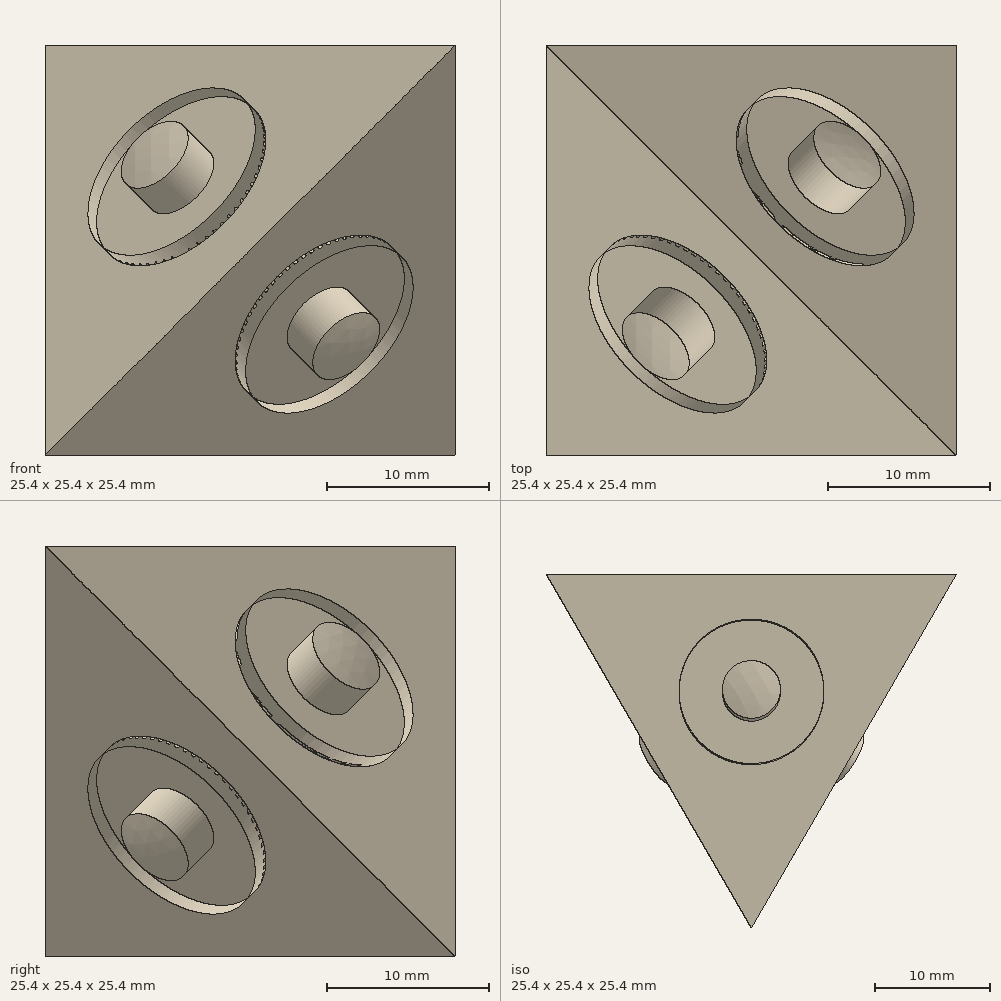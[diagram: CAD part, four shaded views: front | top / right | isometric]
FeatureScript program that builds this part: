
annotation { "Feature Type Name" : "Feature", "Feature Type Description" : "" }
export const myFeature = defineFeature(function(context is Context, id is Id, definition is map)
    precondition{}
    {
        {
            assignVariable(context, id + "F0", {"name" : "d", "anyValue" : .2});
        }
        {
            var Q0;
            Q0=qCreatedBy(makeId("Front.planeOp"),FACE);
            var sketch = newSketch(context, id + "F1", { "sketchPlane" : qUnion([Q0])});
            skCircle(sketch, "E0", {"center": v(0, 0) * mm, "radius": 10.58 * mm});
            skSolve(sketch);
        }
        {
            var Q0;
            Q0=qCreatedBy(makeId("Right.planeOp"),FACE);
            var sketch = newSketch(context, id + "F2", { "sketchPlane" : qUnion([Q0])});
            skCircle(sketch, "E1", {"center": v(0, 0) * mm, "radius": 10.58 * mm});
            skSolve(sketch);
        }
        {
            var Q0;
            Q0=qCreatedBy(makeId("Front.planeOp"),FACE);
            var sketch = newSketch(context, id + "F3", { "sketchPlane" : qUnion([Q0])});
            skLineSegment(sketch, "E2.bottom", {"start": v(12.7, -12.7) * mm, "end": v(-12.7, -12.7) * mm});
            skLineSegment(sketch, "E2.top", {"start": v(12.7, 12.7) * mm, "end": v(-12.7, 12.7) * mm});
            skLineSegment(sketch, "E2.left", {"start": v(12.7, -12.7) * mm, "end": v(12.7, 12.7) * mm});
            skLineSegment(sketch, "E2.right", {"start": v(-12.7, -12.7) * mm, "end": v(-12.7, 12.7) * mm});
            skPoint(sketch, "E2.middle", {"position": v(0, 0) * mm});
            skSolve(sketch);
        }
        {
            var Q0;
            Q0=makeQuery(id+"F3.imprint","IMPRINT",FACE,{"disambiguationData":[TD([[makeQuery(id+"F3.imprint","IMPRINT",EDGE,{"derivedFrom":sQuery(id+"F3.wireOp",EDGE,"E2.bottom")}),-1.0]])]});
            extrude(context, id + "F4", {"entities" : qUnion([Q0]), "endBound" : BoundingType.SYMMETRIC, "depth" : 25.4 * mm, "offsetDistance" : 25.4 * mm});
        }
        {
            var Q0;
            Q0=makeQuery(id+"F4.opExtrude","SWEPT_FACE",FACE,{"disambiguationData":[OSD([sQuery(id+"F3.wireOp",EDGE,"E2.right")])]});
            var sketch = newSketch(context, id + "F5", { "sketchPlane" : qUnion([Q0])});
            skLineSegment(sketch, "E3", {"start": v(-12.7, 12.7) * mm, "end": v(12.7, -12.7) * mm});
            skSolve(sketch);
        }
        {
            var Q0;
            Q0=makeQuery(id+"F4.opExtrude","CAP_FACE",FACE,{"disambiguationData":[OSD([sQuery(id+"F3.wireOp",EDGE,"E2.bottom"),sQuery(id+"F3.wireOp",EDGE,"E2.top"),sQuery(id+"F3.wireOp",EDGE,"E2.left"),sQuery(id+"F3.wireOp",EDGE,"E2.right")])],"isStart":false});
            var sketch = newSketch(context, id + "F6", { "sketchPlane" : qUnion([Q0])});
            skLineSegment(sketch, "E4", {"start": v(-12.7, -12.7) * mm, "end": v(12.7, 12.7) * mm});
            skSolve(sketch);
        }
        {
            var Q0;
            Q0=makeQuery(id+"F4.opExtrude","CAP_FACE",FACE,{"disambiguationData":[OSD([sQuery(id+"F3.wireOp",EDGE,"E2.bottom"),sQuery(id+"F3.wireOp",EDGE,"E2.top"),sQuery(id+"F3.wireOp",EDGE,"E2.left"),sQuery(id+"F3.wireOp",EDGE,"E2.right")])],"isStart":true});
            var sketch = newSketch(context, id + "F7", { "sketchPlane" : qUnion([Q0])});
            skLineSegment(sketch, "E5", {"start": v(12.7, 12.7) * mm, "end": v(-12.7, -12.7) * mm});
            skSolve(sketch);
        }
        {
            var Q0;
            Q0=makeQuery(id+"F4.opExtrude","SWEPT_FACE",FACE,{"disambiguationData":[OSD([sQuery(id+"F3.wireOp",EDGE,"E2.bottom")])]});
            var sketch = newSketch(context, id + "F8", { "sketchPlane" : qUnion([Q0])});
            skLineSegment(sketch, "E6", {"start": v(-12.7, 12.7) * mm, "end": v(12.7, -12.7) * mm});
            skSolve(sketch);
        }
        {
            var Q0;
            Q0=sQuery(id+"F7.wireOp",VERTEX,"E5.start");
            var Q1;
            Q1=sQuery(id+"F8.wireOp",VERTEX,"E6.end");
            var Q2;
            Q2=sQuery(id+"F5.wireOp",VERTEX,"E3.end");
            cPlane(context, id + "F9", {"entities" : qUnion([Q0, Q1, Q2]), "cplaneType" : CPlaneType.THREE_POINT, "offset" : 25.4 * mm, "width" : 152.4 * mm, "height" : 152.4 * mm});
        }
        {
            var Q0;
            Q0=qCreatedBy(id+"F9.planeOp",FACE);
            var sketch = newSketch(context, id + "F10", { "sketchPlane" : qUnion([Q0])});
            skLineSegment(sketch, "E7.bottom", {"start": v(31.97, 29.26) * mm, "end": v(-31.97, 29.26) * mm});
            skLineSegment(sketch, "E7.top", {"start": v(31.97, -34.1) * mm, "end": v(-31.97, -34.1) * mm});
            skLineSegment(sketch, "E7.left", {"start": v(31.97, 29.26) * mm, "end": v(31.97, -34.1) * mm});
            skLineSegment(sketch, "E7.right", {"start": v(-31.97, 29.26) * mm, "end": v(-31.97, -34.1) * mm});
            skPoint(sketch, "E7.middle", {"position": v(0, -2.42) * mm});
            skSolve(sketch);
        }
        {
            var Q0;
            Q0=makeQuery(id+"F10.imprint","IMPRINT",FACE,{"disambiguationData":[TD([[makeQuery(id+"F10.imprint","IMPRINT",EDGE,{"derivedFrom":sQuery(id+"F10.wireOp",EDGE,"E7.bottom")}),1.0]])]});
            extrude(context, id + "F11", {"entities" : qUnion([Q0]), "operationType" : NewBodyOperationType.REMOVE, "oppositeDirection" : true, "depth" : 25.4 * mm, "offsetDistance" : 25.4 * mm});
        }
        {
            var Q0;
            Q0=sQuery(id+"F5.wireOp",VERTEX,"E3.end");
            var Q1;
            Q1=sQuery(id+"F7.wireOp",VERTEX,"E5.start");
            var Q2;
            Q2=sQuery(id+"F6.wireOp",VERTEX,"E4.end");
            cPlane(context, id + "F12", {"entities" : qUnion([Q0, Q1, Q2]), "cplaneType" : CPlaneType.THREE_POINT, "offset" : 25.4 * mm, "width" : 152.4 * mm, "height" : 152.4 * mm});
        }
        {
            var Q0;
            Q0=qCreatedBy(id+"F12.planeOp",FACE);
            var sketch = newSketch(context, id + "F13", { "sketchPlane" : qUnion([Q0])});
            skLineSegment(sketch, "E8.bottom", {"start": v(34.62, 31.3) * mm, "end": v(-34.62, 31.3) * mm});
            skLineSegment(sketch, "E8.top", {"start": v(34.62, -31.3) * mm, "end": v(-34.62, -31.3) * mm});
            skLineSegment(sketch, "E8.left", {"start": v(34.62, 31.3) * mm, "end": v(34.62, -31.3) * mm});
            skLineSegment(sketch, "E8.right", {"start": v(-34.62, 31.3) * mm, "end": v(-34.62, -31.3) * mm});
            skPoint(sketch, "E8.middle", {"position": v(0, 0) * mm});
            skSolve(sketch);
        }
        {
            var Q0;
            Q0=makeQuery(id+"F13.imprint","IMPRINT",FACE,{"disambiguationData":[TD([[makeQuery(id+"F13.imprint","IMPRINT",EDGE,{"derivedFrom":sQuery(id+"F13.wireOp",EDGE,"E8.bottom")}),1.0]])]});
            extrude(context, id + "F14", {"entities" : qUnion([Q0]), "operationType" : NewBodyOperationType.REMOVE, "depth" : 25.4 * mm, "offsetDistance" : 25.4 * mm});
        }
        {
            var Q0;
            Q0=sQuery(id+"F6.wireOp",VERTEX,"E4.end");
            var Q1;
            Q1=sQuery(id+"F8.wireOp",VERTEX,"E6.end");
            var Q2;
            Q2=sQuery(id+"F7.wireOp",VERTEX,"E5.start");
            cPlane(context, id + "F15", {"entities" : qUnion([Q0, Q1, Q2]), "cplaneType" : CPlaneType.THREE_POINT, "offset" : 25.4 * mm, "width" : 152.4 * mm, "height" : 152.4 * mm});
        }
        {
            var Q0;
            Q0=qCreatedBy(id+"F15.planeOp",FACE);
            var sketch = newSketch(context, id + "F16", { "sketchPlane" : qUnion([Q0])});
            skLineSegment(sketch, "E9.bottom", {"start": v(41.74, -29.23) * mm, "end": v(-41.74, -29.23) * mm});
            skLineSegment(sketch, "E9.top", {"start": v(41.74, 32.56) * mm, "end": v(-41.74, 32.56) * mm});
            skLineSegment(sketch, "E9.left", {"start": v(41.74, -29.23) * mm, "end": v(41.74, 32.56) * mm});
            skLineSegment(sketch, "E9.right", {"start": v(-41.74, -29.23) * mm, "end": v(-41.74, 32.56) * mm});
            skPoint(sketch, "E9.middle", {"position": v(0, 1.66) * mm});
            skSolve(sketch);
        }
        {
            var Q0;
            Q0=makeQuery(id+"F16.imprint","IMPRINT",FACE,{"disambiguationData":[TD([[makeQuery(id+"F16.imprint","IMPRINT",EDGE,{"derivedFrom":sQuery(id+"F16.wireOp",EDGE,"E9.bottom")}),-1.0]])]});
            extrude(context, id + "F17", {"entities" : qUnion([Q0]), "operationType" : NewBodyOperationType.REMOVE, "oppositeDirection" : true, "depth" : 25.4 * mm, "offsetDistance" : 25.4 * mm});
        }
        {
            var Q0;
            Q0=sQuery(id+"F5.wireOp",VERTEX,"E3.end");
            var Q1;
            Q1=sQuery(id+"F6.wireOp",VERTEX,"E4.end");
            var Q2;
            Q2=sQuery(id+"F8.wireOp",VERTEX,"E6.end");
            cPlane(context, id + "F18", {"entities" : qUnion([Q0, Q1, Q2]), "cplaneType" : CPlaneType.THREE_POINT, "offset" : 25.4 * mm, "width" : 152.4 * mm, "height" : 152.4 * mm});
        }
        {
            var Q0;
            Q0=qCreatedBy(id+"F18.planeOp",FACE);
            var sketch = newSketch(context, id + "F19", { "sketchPlane" : qUnion([Q0])});
            skLineSegment(sketch, "E10.bottom", {"start": v(47.99, -32.73) * mm, "end": v(-47.99, -32.73) * mm});
            skLineSegment(sketch, "E10.top", {"start": v(47.99, 32.73) * mm, "end": v(-47.99, 32.73) * mm});
            skLineSegment(sketch, "E10.left", {"start": v(47.99, -32.73) * mm, "end": v(47.99, 32.73) * mm});
            skLineSegment(sketch, "E10.right", {"start": v(-47.99, -32.73) * mm, "end": v(-47.99, 32.73) * mm});
            skPoint(sketch, "E10.middle", {"position": v(0, 0) * mm});
            skSolve(sketch);
        }
        {
            var Q0;
            Q0=makeQuery(id+"F19.imprint","IMPRINT",FACE,{"disambiguationData":[TD([[makeQuery(id+"F19.imprint","IMPRINT",EDGE,{"derivedFrom":sQuery(id+"F19.wireOp",EDGE,"E10.bottom")}),-1.0]])]});
            extrude(context, id + "F20", {"entities" : qUnion([Q0]), "operationType" : NewBodyOperationType.REMOVE, "depth" : 25.4 * mm, "offsetDistance" : 25.4 * mm});
        }
        {
            var Q0;
            Q0=makeQuery(id+"F1.imprint","IMPRINT",FACE,{"disambiguationData":[TD([[makeQuery(id+"F1.imprint","IMPRINT",EDGE,{"derivedFrom":sQuery(id+"F1.wireOp",EDGE,"E0")}),1.0]])]});
            var Q1;
            Q1=sQuery(id+"F2.wireOp",EDGE,"E1");
            sweep(context, id + "F21", {"profiles" : qUnion([Q0]), "path" : qUnion([Q1])});
        }
        {
            var Q0;
            Q0=qCreatedBy(id+"F18.planeOp",FACE);
            var sketch = newSketch(context, id + "F22", { "sketchPlane" : qUnion([Q0])});
            skCircle(sketch, "E11", {"center": v(0, 0) * mm, "radius": 6.35 * mm});
            skCircle(sketch, "E12", {"center": v(0, 0) * mm, "radius": 2.54 * mm});
            skSolve(sketch);
        }
        {
            var Q0;
            Q0 = qSketchRegion(id + "F22", true);
            extrude(context, id + "F23", {"entities" : qUnion([Q0]), "operationType" : NewBodyOperationType.REMOVE, "depth" : 25.4 * mm, "offsetDistance" : 25.4 * mm});
        }
        {
            var Q0;
            Q0=qCreatedBy(id+"F15.planeOp",FACE);
            var sketch = newSketch(context, id + "F24", { "sketchPlane" : qUnion([Q0])});
            skCircle(sketch, "E13", {"center": v(0, 0) * mm, "radius": 6.35 * mm});
            skCircle(sketch, "E14", {"center": v(0, 0) * mm, "radius": 2.54 * mm});
            skSolve(sketch);
        }
        {
            var Q0;
            Q0=qCreatedBy(id+"F12.planeOp",FACE);
            var sketch = newSketch(context, id + "F25", { "sketchPlane" : qUnion([Q0])});
            skCircle(sketch, "E15", {"center": v(0, 0) * mm, "radius": 6.35 * mm});
            skCircle(sketch, "E16", {"center": v(0, 0) * mm, "radius": 2.54 * mm});
            skSolve(sketch);
        }
        {
            var Q0;
            Q0=qCreatedBy(id+"F9.planeOp",FACE);
            var sketch = newSketch(context, id + "F26", { "sketchPlane" : qUnion([Q0])});
            skCircle(sketch, "E17", {"center": v(0, 0) * mm, "radius": 6.35 * mm});
            skCircle(sketch, "E18", {"center": v(0, 0) * mm, "radius": 2.54 * mm});
            skSolve(sketch);
        }
        {
            var Q0;
            Q0 = qSketchRegion(id + "F24", true);
            extrude(context, id + "F27", {"entities" : qUnion([Q0]), "operationType" : NewBodyOperationType.REMOVE, "oppositeDirection" : true, "depth" : 25.4 * mm, "offsetDistance" : 25.4 * mm});
        }
        {
            var Q0;
            Q0 = qSketchRegion(id + "F25", true);
            extrude(context, id + "F28", {"entities" : qUnion([Q0]), "operationType" : NewBodyOperationType.REMOVE, "depth" : 25.4 * mm, "offsetDistance" : 25.4 * mm});
        }
        {
            var Q0;
            Q0 = qSketchRegion(id + "F26", true);
            extrude(context, id + "F29", {"entities" : qUnion([Q0]), "operationType" : NewBodyOperationType.REMOVE, "oppositeDirection" : true, "depth" : 25.4 * mm, "offsetDistance" : 25.4 * mm});
        }
        {
            var Q0;
            Q0=makeQuery(id+"F11.boolean.opBoolean","COPY",FACE,{"derivedFrom":makeQuery(id+"F11.opExtrude","CAP_FACE",FACE,{"disambiguationData":[OSD([sQuery(id+"F10.wireOp",EDGE,"E7.bottom"),sQuery(id+"F10.wireOp",EDGE,"E7.top"),sQuery(id+"F10.wireOp",EDGE,"E7.left"),sQuery(id+"F10.wireOp",EDGE,"E7.right")])],"isStart":true})});
            var sketch = newSketch(context, id + "F30", { "sketchPlane" : qUnion([Q0])});
            skLineSegment(sketch, "E19", {"start": v(20.74, 0) * mm, "end": v(-10.37, 17.96) * mm});
            skLineSegment(sketch, "E20", {"start": v(-10.37, 17.96) * mm, "end": v(-10.37, -17.96) * mm});
            skLineSegment(sketch, "E21", {"start": v(-10.37, -17.96) * mm, "end": v(20.74, 0) * mm});
            skSolve(sketch);
        }
        {
            var Q0;
            Q0=sQuery(id+"F30.wireOp",EDGE,"E19");
            var Q1;
            Q1=sQuery(id+"F30.wireOp",VERTEX,"E20.end");
            loft(context, id + "F31", {"bodyType" : ToolBodyType.SURFACE, "wireProfilesArray" : [{ "wireProfileEntities" : qUnion([Q0]) }, { "wireProfileEntities" : qUnion([Q1]) }]});
        }
        {
            var Q0;
            Q0 = qSketchRegion(id + "F24", true);
            extrude(context, id + "F32", {"entities" : qUnion([Q0]), "oppositeDirection" : true, "depth" : (getVariable(context, 'd')) * mm, "offsetDistance" : 25.4 * mm});
        }
        {
            var Q0;
            Q0 = qSketchRegion(id + "F25", true);
            extrude(context, id + "F33", {"entities" : qUnion([Q0]), "depth" : (getVariable(context, 'd')) * mm, "offsetDistance" : 25.4 * mm});
        }
        {
            var Q0;
            Q0 = qSketchRegion(id + "F26", true);
            extrude(context, id + "F34", {"entities" : qUnion([Q0]), "oppositeDirection" : true, "depth" : (getVariable(context, 'd')) * mm, "offsetDistance" : 25.4 * mm});
        }
        {
            var Q0;
            Q0 = qSketchRegion(id + "F22", true);
            extrude(context, id + "F35", {"entities" : qUnion([Q0]), "depth" : (getVariable(context, 'd')) * mm, "offsetDistance" : 25.4 * mm});
        }
        {
            var Q0;
            Q0=makeQuery(id+"F20.boolean.opBoolean","COPY",FACE,{"derivedFrom":makeQuery(id+"F20.opExtrude","CAP_FACE",FACE,{"disambiguationData":[OSD([sQuery(id+"F19.wireOp",EDGE,"E10.bottom"),sQuery(id+"F19.wireOp",EDGE,"E10.top"),sQuery(id+"F19.wireOp",EDGE,"E10.left"),sQuery(id+"F19.wireOp",EDGE,"E10.right")])],"isStart":true})});
            var sketch = newSketch(context, id + "F36", { "sketchPlane" : qUnion([Q0])});
            skLineSegment(sketch, "E22", {"start": v(-10.37, 17.96) * mm, "end": v(-10.37, -17.96) * mm});
            skLineSegment(sketch, "E23", {"start": v(-10.37, -17.96) * mm, "end": v(20.74, 0) * mm});
            skLineSegment(sketch, "E24", {"start": v(20.74, 0) * mm, "end": v(-10.37, 17.96) * mm});
            skSolve(sketch);
        }
        {
            var Q0;
            Q0=sQuery(id+"F36.wireOp",EDGE,"E23");
            var Q1;
            Q1=sQuery(id+"F36.wireOp",VERTEX,"E22.start");
            var Q2;
            Q2=sQuery(id+"F36.wireOp",EDGE,"E24");
            var Q3;
            Q3=sQuery(id+"F36.wireOp",EDGE,"E22");
            loft(context, id + "F37", {"bodyType" : ToolBodyType.SURFACE, "addGuides" : true, "wireProfilesArray" : [{ "wireProfileEntities" : qUnion([Q0]) }, { "wireProfileEntities" : qUnion([Q1]) }], "guidesArray" : [{ "guideEntities" : qUnion([Q2]), "guideDerivativeType" : LoftGuideDerivativeType.DEFAULT, "guideDerivativeMagnitude" : 1 }, { "guideEntities" : qUnion([Q3]), "guideDerivativeType" : LoftGuideDerivativeType.DEFAULT, "guideDerivativeMagnitude" : 1 }]});
        }
        {
            var Q0;
            Q0=makeQuery(id+"F17.boolean.opBoolean","COPY",FACE,{"derivedFrom":makeQuery(id+"F17.opExtrude","CAP_FACE",FACE,{"disambiguationData":[OSD([sQuery(id+"F16.wireOp",EDGE,"E9.bottom"),sQuery(id+"F16.wireOp",EDGE,"E9.top"),sQuery(id+"F16.wireOp",EDGE,"E9.left"),sQuery(id+"F16.wireOp",EDGE,"E9.right")])],"isStart":true})});
            var sketch = newSketch(context, id + "F38", { "sketchPlane" : qUnion([Q0])});
            skLineSegment(sketch, "E25", {"start": v(20.74, 0) * mm, "end": v(-10.37, -17.96) * mm});
            skLineSegment(sketch, "E26", {"start": v(-10.37, -17.96) * mm, "end": v(-10.37, 17.96) * mm});
            skLineSegment(sketch, "E27", {"start": v(20.74, 0) * mm, "end": v(-10.37, 17.96) * mm});
            skSolve(sketch);
        }
        {
            var Q0;
            Q0=sQuery(id+"F38.wireOp",EDGE,"E25");
            var Q1;
            Q1=sQuery(id+"F38.wireOp",VERTEX,"E27.end");
            var Q2;
            Q2=sQuery(id+"F38.wireOp",EDGE,"E27");
            var Q3;
            Q3=sQuery(id+"F38.wireOp",EDGE,"E26");
            loft(context, id + "F39", {"bodyType" : ToolBodyType.SURFACE, "addGuides" : true, "wireProfilesArray" : [{ "wireProfileEntities" : qUnion([Q0]) }, { "wireProfileEntities" : qUnion([Q1]) }], "guidesArray" : [{ "guideEntities" : qUnion([Q2]), "guideDerivativeType" : LoftGuideDerivativeType.DEFAULT, "guideDerivativeMagnitude" : 1 }, { "guideEntities" : qUnion([Q3]), "guideDerivativeType" : LoftGuideDerivativeType.DEFAULT, "guideDerivativeMagnitude" : 1 }]});
        }
        {
            var Q0;
            Q0=sQuery(id+"F38.wireOp",EDGE,"E25");
            var Q1;
            Q1=sQuery(id+"F38.wireOp",VERTEX,"E26.end");
            var Q2;
            Q2=sQuery(id+"F38.wireOp",EDGE,"E27");
            var Q3;
            Q3=sQuery(id+"F38.wireOp",EDGE,"E26");
            loft(context, id + "F40", {"bodyType" : ToolBodyType.SURFACE, "addGuides" : true, "wireProfilesArray" : [{ "wireProfileEntities" : qUnion([Q0]) }, { "wireProfileEntities" : qUnion([Q1]) }], "guidesArray" : [{ "guideEntities" : qUnion([Q2]), "guideDerivativeType" : LoftGuideDerivativeType.DEFAULT, "guideDerivativeMagnitude" : 1 }, { "guideEntities" : qUnion([Q3]), "guideDerivativeType" : LoftGuideDerivativeType.DEFAULT, "guideDerivativeMagnitude" : 1 }]});
        }
        {
            var Q0;
            Q0=makeQuery(id+"F36.imprint","IMPRINT",FACE,{"disambiguationData":[TD([[makeQuery(id+"F36.imprint","IMPRINT",EDGE,{"derivedFrom":sQuery(id+"F36.wireOp",EDGE,"E22")}),1.0]])]});
            var Q1;
            Q1=sQuery(id+"F36.wireOp",EDGE,"E24");
            var Q2;
            Q2=sQuery(id+"F36.wireOp",VERTEX,"E23.start");
            var Q3;
            Q3=sQuery(id+"F36.wireOp",EDGE,"E23");
            var Q4;
            Q4=sQuery(id+"F36.wireOp",EDGE,"E22");
            loft(context, id + "F41", {"bodyType" : ToolBodyType.SURFACE, "addGuides" : true, "sheetProfilesArray" : [{ "sheetProfileEntities" : qUnion([Q0]) }], "wireProfilesArray" : [{ "wireProfileEntities" : qUnion([Q1]) }, { "wireProfileEntities" : qUnion([Q2]) }], "guidesArray" : [{ "guideEntities" : qUnion([Q3]), "guideDerivativeType" : LoftGuideDerivativeType.DEFAULT, "guideDerivativeMagnitude" : 1 }, { "guideEntities" : qUnion([Q4]), "guideDerivativeType" : LoftGuideDerivativeType.DEFAULT, "guideDerivativeMagnitude" : 1 }]});
        }
        {
            var Q0;
            Q0=sQuery(id+"F30.wireOp",VERTEX,"E19.start");
            var Q1;
            Q1=sQuery(id+"F30.wireOp",EDGE,"E19");
            var Q2;
            Q2=sQuery(id+"F30.wireOp",VERTEX,"E21.start");
            var Q3;
            Q3=sQuery(id+"F30.wireOp",EDGE,"E21");
            var Q4;
            Q4=sQuery(id+"F30.wireOp",EDGE,"E20");
            loft(context, id + "F42", {"bodyType" : ToolBodyType.SURFACE, "addGuides" : true, "sheetProfilesArray" : [{ "sheetProfileEntities" : qUnion([Q0]) }], "wireProfilesArray" : [{ "wireProfileEntities" : qUnion([Q1]) }, { "wireProfileEntities" : qUnion([Q2]) }], "guidesArray" : [{ "guideEntities" : qUnion([Q3]), "guideDerivativeType" : LoftGuideDerivativeType.DEFAULT, "guideDerivativeMagnitude" : 1 }, { "guideEntities" : qUnion([Q4]), "guideDerivativeType" : LoftGuideDerivativeType.DEFAULT, "guideDerivativeMagnitude" : 1 }]});
        }
        {
            var Q0;
            Q0=sQuery(id+"F36.wireOp",EDGE,"E24");
            var Q1;
            Q1=sQuery(id+"F36.wireOp",VERTEX,"E23.start");
            var Q2;
            Q2=sQuery(id+"F36.wireOp",EDGE,"E22");
            var Q3;
            Q3=sQuery(id+"F36.wireOp",EDGE,"E23");
            loft(context, id + "F43", {"bodyType" : ToolBodyType.SURFACE, "addGuides" : true, "wireProfilesArray" : [{ "wireProfileEntities" : qUnion([Q0]) }, { "wireProfileEntities" : qUnion([Q1]) }], "guidesArray" : [{ "guideEntities" : qUnion([Q2]), "guideDerivativeType" : LoftGuideDerivativeType.DEFAULT, "guideDerivativeMagnitude" : 1 }, { "guideEntities" : qUnion([Q3]), "guideDerivativeType" : LoftGuideDerivativeType.DEFAULT, "guideDerivativeMagnitude" : 1 }]});
        }
        {
            var Q0;
            Q0=makeQuery(id+"F14.boolean.opBoolean","COPY",FACE,{"derivedFrom":makeQuery(id+"F14.opExtrude","CAP_FACE",FACE,{"disambiguationData":[OSD([sQuery(id+"F13.wireOp",EDGE,"E8.bottom"),sQuery(id+"F13.wireOp",EDGE,"E8.top"),sQuery(id+"F13.wireOp",EDGE,"E8.left"),sQuery(id+"F13.wireOp",EDGE,"E8.right")])],"isStart":true})});
            var sketch = newSketch(context, id + "F44", { "sketchPlane" : qUnion([Q0])});
            skLineSegment(sketch, "E28", {"start": v(-20.74, 0) * mm, "end": v(10.37, -17.96) * mm});
            skLineSegment(sketch, "E29", {"start": v(10.37, -17.96) * mm, "end": v(10.37, 17.96) * mm});
            skLineSegment(sketch, "E30", {"start": v(10.37, 17.96) * mm, "end": v(-20.74, 0) * mm});
            skSolve(sketch);
        }
        {
            var Q0;
            Q0=makeQuery(id+"F44.imprint","IMPRINT",FACE,{"disambiguationData":[TD([[makeQuery(id+"F44.imprint","IMPRINT",EDGE,{"derivedFrom":sQuery(id+"F44.wireOp",EDGE,"E28")}),-1.0]])]});
            var Q1;
            Q1=sQuery(id+"F44.wireOp",EDGE,"E28");
            var Q2;
            Q2=sQuery(id+"F44.wireOp",VERTEX,"E29.end");
            var Q3;
            Q3=sQuery(id+"F44.wireOp",EDGE,"E30");
            var Q4;
            Q4=sQuery(id+"F44.wireOp",EDGE,"E29");
            loft(context, id + "F45", {"bodyType" : ToolBodyType.SURFACE, "addGuides" : true, "sheetProfilesArray" : [{ "sheetProfileEntities" : qUnion([Q0]) }], "wireProfilesArray" : [{ "wireProfileEntities" : qUnion([Q1]) }, { "wireProfileEntities" : qUnion([Q2]) }], "guidesArray" : [{ "guideEntities" : qUnion([Q3]), "guideDerivativeType" : LoftGuideDerivativeType.DEFAULT, "guideDerivativeMagnitude" : 1 }, { "guideEntities" : qUnion([Q4]), "guideDerivativeType" : LoftGuideDerivativeType.DEFAULT, "guideDerivativeMagnitude" : 1 }]});
        }
        {
            var Q0;
            Q0=makeQuery(id+"F14.boolean.opBoolean","COPY",FACE,{"derivedFrom":makeQuery(id+"F14.opExtrude","CAP_FACE",FACE,{"disambiguationData":[OSD([sQuery(id+"F13.wireOp",EDGE,"E8.bottom"),sQuery(id+"F13.wireOp",EDGE,"E8.top"),sQuery(id+"F13.wireOp",EDGE,"E8.left"),sQuery(id+"F13.wireOp",EDGE,"E8.right")])],"isStart":true})});
            var sketch = newSketch(context, id + "F46", { "sketchPlane" : qUnion([Q0])});
            skLineSegment(sketch, "E31", {"start": v(-20.74, 0) * mm, "end": v(10.37, 17.96) * mm});
            skLineSegment(sketch, "E32", {"start": v(10.37, 17.96) * mm, "end": v(10.37, -17.96) * mm});
            skLineSegment(sketch, "E33", {"start": v(10.37, -17.96) * mm, "end": v(-20.74, 0) * mm});
            skSolve(sketch);
        }
        {
            var Q0;
            Q0=sQuery(id+"F46.wireOp",VERTEX,"E32.end");
            var Q1;
            Q1=sQuery(id+"F46.wireOp",EDGE,"E31");
            var Q2;
            Q2=sQuery(id+"F46.wireOp",VERTEX,"E32.end");
            var Q3;
            Q3=sQuery(id+"F46.wireOp",EDGE,"E33");
            var Q4;
            Q4=sQuery(id+"F46.wireOp",EDGE,"E32");
            loft(context, id + "F47", {"bodyType" : ToolBodyType.SURFACE, "addGuides" : true, "sheetProfilesArray" : [{ "sheetProfileEntities" : qUnion([Q0]) }], "wireProfilesArray" : [{ "wireProfileEntities" : qUnion([Q1]) }, { "wireProfileEntities" : qUnion([Q2]) }], "guidesArray" : [{ "guideEntities" : qUnion([Q3]), "guideDerivativeType" : LoftGuideDerivativeType.DEFAULT, "guideDerivativeMagnitude" : 1 }, { "guideEntities" : qUnion([Q4]), "guideDerivativeType" : LoftGuideDerivativeType.DEFAULT, "guideDerivativeMagnitude" : 1 }]});
        }
        {
            var Q0;
            Q0=makeQuery(id+"F17.boolean.opBoolean","COPY",FACE,{"derivedFrom":makeQuery(id+"F17.opExtrude","CAP_FACE",FACE,{"disambiguationData":[OSD([sQuery(id+"F16.wireOp",EDGE,"E9.bottom"),sQuery(id+"F16.wireOp",EDGE,"E9.top"),sQuery(id+"F16.wireOp",EDGE,"E9.left"),sQuery(id+"F16.wireOp",EDGE,"E9.right")])],"isStart":true})});
            var sketch = newSketch(context, id + "F48", { "sketchPlane" : qUnion([Q0])});
            skLineSegment(sketch, "E34", {"start": v(-10.37, 17.96) * mm, "end": v(20.74, 0) * mm});
            skLineSegment(sketch, "E35", {"start": v(20.74, 0) * mm, "end": v(-10.37, -17.96) * mm});
            skLineSegment(sketch, "E36", {"start": v(-10.37, -17.96) * mm, "end": v(-10.37, 17.96) * mm});
            skSolve(sketch);
        }
        {
            var Q0;
            Q0=sQuery(id+"F48.wireOp",EDGE,"E36");
            var Q1;
            Q1=sQuery(id+"F48.wireOp",VERTEX,"E34.end");
            var Q2;
            Q2=sQuery(id+"F48.wireOp",EDGE,"E34");
            var Q3;
            Q3=sQuery(id+"F48.wireOp",EDGE,"E35");
            loft(context, id + "F49", {"bodyType" : ToolBodyType.SURFACE, "addGuides" : true, "wireProfilesArray" : [{ "wireProfileEntities" : qUnion([Q0]) }, { "wireProfileEntities" : qUnion([Q1]) }], "guidesArray" : [{ "guideEntities" : qUnion([Q2]), "guideDerivativeType" : LoftGuideDerivativeType.DEFAULT, "guideDerivativeMagnitude" : 1 }, { "guideEntities" : qUnion([Q3]), "guideDerivativeType" : LoftGuideDerivativeType.DEFAULT, "guideDerivativeMagnitude" : 1 }]});
        }
        {
            var Q0;
            Q0=makeQuery(id+"F11.boolean.opBoolean","COPY",FACE,{"derivedFrom":makeQuery(id+"F11.opExtrude","CAP_FACE",FACE,{"disambiguationData":[OSD([sQuery(id+"F10.wireOp",EDGE,"E7.bottom"),sQuery(id+"F10.wireOp",EDGE,"E7.top"),sQuery(id+"F10.wireOp",EDGE,"E7.left"),sQuery(id+"F10.wireOp",EDGE,"E7.right")])],"isStart":true})});
            var sketch = newSketch(context, id + "F50", { "sketchPlane" : qUnion([Q0])});
            skLineSegment(sketch, "E37", {"start": v(20.74, 0) * mm, "end": v(-10.37, 17.96) * mm});
            skLineSegment(sketch, "E38", {"start": v(-10.37, 17.96) * mm, "end": v(-10.37, -17.96) * mm});
            skLineSegment(sketch, "E39", {"start": v(-10.37, -17.96) * mm, "end": v(20.74, 0) * mm});
            skSolve(sketch);
        }
        {
            var Q0;
            Q0=sQuery(id+"F50.wireOp",EDGE,"E39");
            var Q1;
            Q1=sQuery(id+"F50.wireOp",VERTEX,"E37.end");
            var Q2;
            Q2=sQuery(id+"F50.wireOp",EDGE,"E37");
            var Q3;
            Q3=sQuery(id+"F50.wireOp",EDGE,"E38");
            loft(context, id + "F51", {"bodyType" : ToolBodyType.SURFACE, "addGuides" : true, "wireProfilesArray" : [{ "wireProfileEntities" : qUnion([Q0]) }, { "wireProfileEntities" : qUnion([Q1]) }], "guidesArray" : [{ "guideEntities" : qUnion([Q2]), "guideDerivativeType" : LoftGuideDerivativeType.DEFAULT, "guideDerivativeMagnitude" : 1 }, { "guideEntities" : qUnion([Q3]), "guideDerivativeType" : LoftGuideDerivativeType.DEFAULT, "guideDerivativeMagnitude" : 1 }]});
        }
    });
